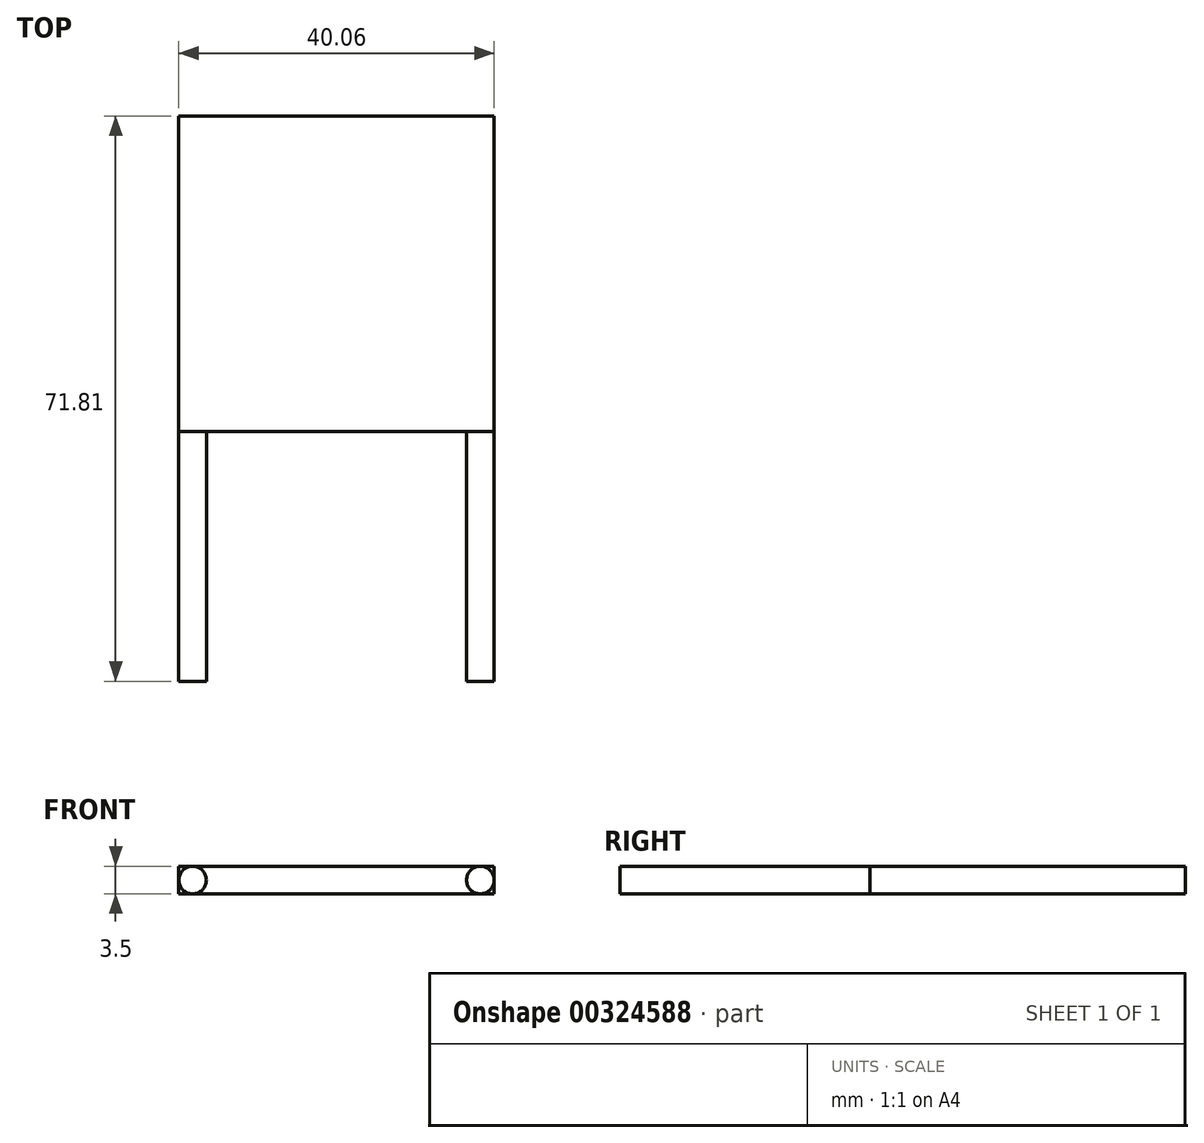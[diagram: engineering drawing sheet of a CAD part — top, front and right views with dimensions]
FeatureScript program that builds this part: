
annotation { "Feature Type Name" : "Feature", "Feature Type Description" : "" }
export const myFeature = defineFeature(function(context is Context, id is Id, definition is map)
    precondition{}
    {
        {
            var Q0;
            Q0=qCreatedBy(makeId("Top.planeOp"),FACE);
            var sketch = newSketch(context, id + "F0", { "sketchPlane" : qUnion([Q0])});
            skLineSegment(sketch, "E0.bottom", {"start": v(-20.03, 20.03) * mm, "end": v(20.03, 20.03) * mm});
            skLineSegment(sketch, "E0.top", {"start": v(-20.03, -20.03) * mm, "end": v(20.03, -20.03) * mm});
            skLineSegment(sketch, "E0.left", {"start": v(-20.03, 20.03) * mm, "end": v(-20.03, -20.03) * mm});
            skLineSegment(sketch, "E0.right", {"start": v(20.03, 20.03) * mm, "end": v(20.03, -20.03) * mm});
            skSolve(sketch);
        }
        {
            var Q0;
            Q0 = qSketchRegion(id + "F0", true);
            extrude(context, id + "F1", {"entities" : qUnion([Q0]), "endBound" : BoundingType.SYMMETRIC, "depth" : 3.5 * mm});
        }
        {
            var Q0;
            Q0=makeQuery(id+"FSMqDiYDhyWJf5a_1.boolean.opBoolean","MERGE",EDGE,{"derivedFrom":[makeQuery(id+"F1.opExtrude","CAP_EDGE",EDGE,{"disambiguationData":[OSD([sQuery(id+"F0.wireOp",EDGE,"E0.top")])],"isStart":false}),makeQuery(id+"FSMqDiYDhyWJf5a_1.opExtrude","SWEPT_EDGE",EDGE,{"disambiguationData":[OSD([sQuery(id+"F0.wireOp",EDGE,"E0.right"),sQuery(id+"FhcF0n7VCXojbJP_1.wireOp",EDGE,"feC9X1nc-c9Re-8DIc-HzV5-JS5RSEZrAhoW"),sQuery(id+"FhcF0n7VCXojbJP_1.wireOp",EDGE,"k44YmHcH-xRwY-iCgy-wNGP-cQqQi5s3QQdF")])]})]});
            cPlane(context, id + "F2", {"entities" : qUnion([Q0]), "cplaneType" : CPlaneType.LINE_ANGLE, "offset" : 25.4 * mm, "angle" : 0 * degree, "width" : 152.4 * mm, "height" : 152.4 * mm});
        }
        {
            var Q0;
            Q0=qCreatedBy(id+"F2.planeOp",FACE);
            var sketch = newSketch(context, id + "F3", { "sketchPlane" : qUnion([Q0])});
            skCircle(sketch, "E1", {"center": v(-18.28, 0) * mm, "radius": 1.75 * mm});
            skCircle(sketch, "E2", {"center": v(18.28, 0) * mm, "radius": 1.75 * mm});
            skSolve(sketch);
        }
        {
            var Q0;
            Q0 = qSketchRegion(id + "F3", true);
            extrude(context, id + "F4", {"entities" : qUnion([Q0]), "operationType" : NewBodyOperationType.ADD, "oppositeDirection" : true, "depth" : 31.75 * mm});
        }
        {
            var Q0;
            Q0=makeQuery(id+"F1.opExtrude","CAP_FACE",FACE,{"disambiguationData":[OSD([sQuery(id+"F0.wireOp",EDGE,"E0.bottom"),sQuery(id+"F0.wireOp",EDGE,"E0.top"),sQuery(id+"F0.wireOp",EDGE,"E0.left"),sQuery(id+"F0.wireOp",EDGE,"E0.right")])],"isStart":false});
            var sketch = newSketch(context, id + "F5", { "sketchPlane" : qUnion([Q0])});
            skLineSegment(sketch, "E3.bottom", {"start": v(-20.03, 20.03) * mm, "end": v(20.03, 20.03) * mm});
            skLineSegment(sketch, "E3.top", {"start": v(-20.03, -20.03) * mm, "end": v(20.03, -20.03) * mm});
            skLineSegment(sketch, "E3.left", {"start": v(-20.03, 20.03) * mm, "end": v(-20.03, -20.03) * mm});
            skLineSegment(sketch, "E3.right", {"start": v(20.03, 20.03) * mm, "end": v(20.03, -20.03) * mm});
            skSolve(sketch);
        }
        {
            var Q0;
            Q0 = qSketchRegion(id + "F5", true);
            extrude(context, id + "F6", {"entities" : qUnion([Q0]), "depth" : ((1 / 25.4) / 2) * mm});
        }
        {
            var Q0;
            Q0=makeQuery(id+"FSMqDiYDhyWJf5a_1.boolean.opBoolean","MERGE",FACE,{"derivedFrom":[makeQuery(id+"F1.opExtrude","CAP_FACE",FACE,{"disambiguationData":[OSD([sQuery(id+"F0.wireOp",EDGE,"E0.bottom"),sQuery(id+"F0.wireOp",EDGE,"E0.top"),sQuery(id+"F0.wireOp",EDGE,"E0.left"),sQuery(id+"F0.wireOp",EDGE,"E0.right")])],"isStart":true}),makeQuery(id+"FSMqDiYDhyWJf5a_1.opExtrude","SWEPT_FACE",FACE,{"disambiguationData":[OSD([sQuery(id+"FhcF0n7VCXojbJP_1.wireOp",EDGE,"aOYyAAMc-cLNu-rMrM-1cw8-kaTzFA0LWoYL")])]})]});
            var sketch = newSketch(context, id + "F7", { "sketchPlane" : qUnion([Q0])});
            skLineSegment(sketch, "E4.bottom", {"start": v(-20.03, 24.04) * mm, "end": v(20.03, 24.04) * mm});
            skLineSegment(sketch, "E4.top", {"start": v(-20.03, -20.03) * mm, "end": v(20.03, -20.03) * mm});
            skLineSegment(sketch, "E4.left", {"start": v(-20.03, 24.04) * mm, "end": v(-20.03, -20.03) * mm});
            skLineSegment(sketch, "E4.right", {"start": v(20.03, 24.04) * mm, "end": v(20.03, -20.03) * mm});
            skSolve(sketch);
        }
        {
            var Q0;
            Q0 = qSketchRegion(id + "F7", true);
            extrude(context, id + "F8", {"entities" : qUnion([Q0]), "depth" : ((1 / 25.4) / 2) * mm});
        }
        {
            var Q0;
            Q0=makeQuery(id+"F6.opExtrude","SWEPT_BODY",BODY,{"disambiguationData":[OSD([sQuery(id+"F5.wireOp",EDGE,"E3.bottom"),sQuery(id+"F5.wireOp",EDGE,"E3.top"),sQuery(id+"F5.wireOp",EDGE,"E3.left"),sQuery(id+"F5.wireOp",EDGE,"E3.right")])]});
            deleteBodies(context, id + "F9", {"entities" : qUnion([Q0])});
        }
        {
            var Q0;
            Q0=makeQuery(id+"F8.opExtrude","SWEPT_BODY",BODY,{"disambiguationData":[OSD([sQuery(id+"F7.wireOp",EDGE,"E4.bottom"),sQuery(id+"F7.wireOp",EDGE,"E4.top"),sQuery(id+"F7.wireOp",EDGE,"E4.left"),sQuery(id+"F7.wireOp",EDGE,"E4.right")])]});
            deleteBodies(context, id + "F10", {"entities" : qUnion([Q0])});
        }
    });
